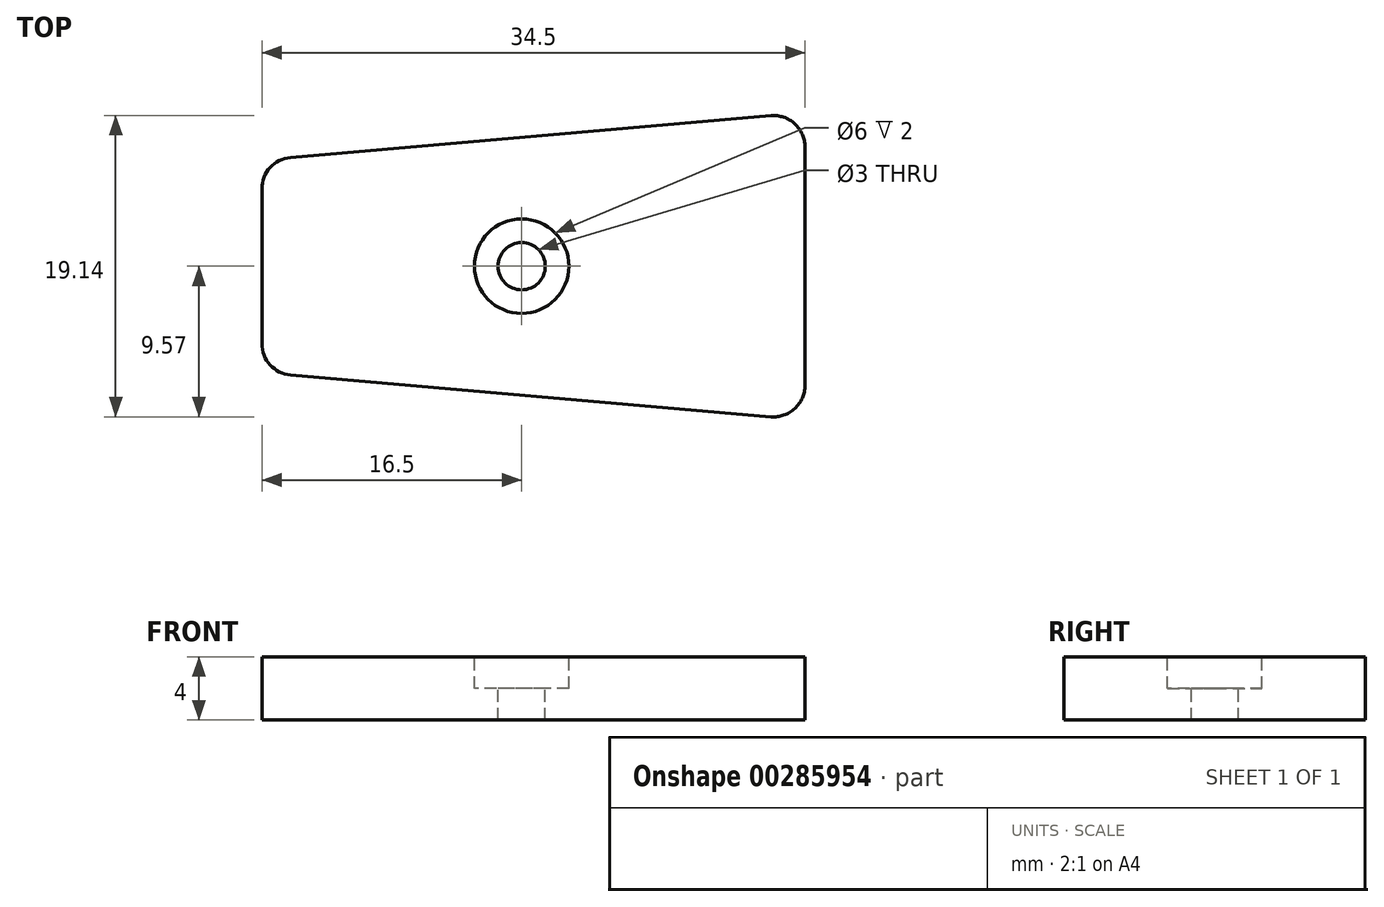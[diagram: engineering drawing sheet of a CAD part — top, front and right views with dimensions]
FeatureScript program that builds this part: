
annotation { "Feature Type Name" : "Feature", "Feature Type Description" : "" }
export const myFeature = defineFeature(function(context is Context, id is Id, definition is map)
    precondition{}
    {
        {
            var Q0;
            Q0=qCreatedBy(makeId("Top.planeOp"),FACE);
            var sketch = newSketch(context, id + "F0", { "sketchPlane" : qUnion([Q0])});
            skLineSegment(sketch, "E0", {"start": v(34.5, 19.5) * mm, "end": v(34.5, 0) * mm});
            skLineSegment(sketch, "E1", {"start": v(0, 3) * mm, "end": v(34.5, 0) * mm});
            skLineSegment(sketch, "E2", {"start": v(0, 16.5) * mm, "end": v(34.5, 19.5) * mm});
            skLineSegment(sketch, "E3", {"start": v(0, 16.5) * mm, "end": v(0, 3) * mm});
            skSolve(sketch);
        }
        {
            var Q0;
            Q0=makeQuery(id+"F0.imprint","IMPRINT",FACE,{"disambiguationData":[TD([[makeQuery(id+"F0.imprint","IMPRINT",EDGE,{"derivedFrom":sQuery(id+"F0.wireOp",EDGE,"E0")}),-1.0]])]});
            extrude(context, id + "F1", {"entities" : qUnion([Q0]), "depth" : 4 * mm});
        }
        {
            var Q0;
            Q0=makeQuery(id+"F1.opExtrude","CAP_FACE",FACE,{"disambiguationData":[OSD([sQuery(id+"F0.wireOp",EDGE,"E0"),sQuery(id+"F0.wireOp",EDGE,"E1"),sQuery(id+"F0.wireOp",EDGE,"E2"),sQuery(id+"F0.wireOp",EDGE,"E3")])],"isStart":false});
            var sketch = newSketch(context, id + "F2", { "sketchPlane" : qUnion([Q0])});
            skPoint(sketch, "E4", {"position": v(16.5, 9.75) * mm});
            skCircle(sketch, "E5", {"center": v(16.5, 9.75) * mm, "radius": 1.5 * mm});
            skCircle(sketch, "E6", {"center": v(16.5, 9.75) * mm, "radius": 3 * mm});
            skSolve(sketch);
        }
        {
            var Q0;
            Q0=makeQuery(id+"F2.imprint","IMPRINT",FACE,{"disambiguationData":[TD([[makeQuery(id+"F2.imprint","IMPRINT",EDGE,{"derivedFrom":sQuery(id+"F2.wireOp",EDGE,"E5")}),-1.0]])]});
            extrude(context, id + "F3", {"entities" : qUnion([Q0]), "operationType" : NewBodyOperationType.REMOVE, "oppositeDirection" : true, "depth" : 2 * mm});
        }
        {
            var Q0;
            Q0=makeQuery(id+"F3.boolean.opBoolean","SPLIT",FACE,{"disambiguationData":[TD([makeQuery(id+"F3.opExtrude","SWEPT_FACE",FACE,{"disambiguationData":[OSD([sQuery(id+"F2.wireOp",EDGE,"E5")])]})])],"derivedFrom":makeQuery(id+"F1.opExtrude","CAP_FACE",FACE,{"disambiguationData":[OSD([sQuery(id+"F0.wireOp",EDGE,"E0"),sQuery(id+"F0.wireOp",EDGE,"E1"),sQuery(id+"F0.wireOp",EDGE,"E2"),sQuery(id+"F0.wireOp",EDGE,"E3")])],"isStart":false})});
            extrude(context, id + "F4", {"entities" : qUnion([Q0]), "operationType" : NewBodyOperationType.REMOVE, "oppositeDirection" : true, "depth" : 4 * mm});
        }
        {
            var Q0;
            Q0=makeQuery(id+"F1.opExtrude","SWEPT_EDGE",EDGE,{"disambiguationData":[OSD([sQuery(id+"F0.wireOp",EDGE,"E0"),sQuery(id+"F0.wireOp",EDGE,"E1")])]});
            fillet(context, id + "F5", {"entities" : qUnion([Q0]), "radius" : 2 * mm, "tangentPropagation" : true, "allowEdgeOverflow" : false});
        }
        {
            var Q0;
            Q0=makeQuery(id+"F1.opExtrude","SWEPT_EDGE",EDGE,{"disambiguationData":[OSD([sQuery(id+"F0.wireOp",EDGE,"E0"),sQuery(id+"F0.wireOp",EDGE,"E2")])]});
            fillet(context, id + "F6", {"entities" : qUnion([Q0]), "radius" : 2 * mm, "tangentPropagation" : true, "allowEdgeOverflow" : false});
        }
        {
            var Q0;
            Q0=makeQuery(id+"F1.opExtrude","SWEPT_EDGE",EDGE,{"disambiguationData":[OSD([sQuery(id+"F0.wireOp",EDGE,"E2"),sQuery(id+"F0.wireOp",EDGE,"E3")])]});
            fillet(context, id + "F7", {"entities" : qUnion([Q0]), "radius" : 2 * mm, "tangentPropagation" : true, "allowEdgeOverflow" : false});
        }
        {
            var Q0;
            Q0=makeQuery(id+"F1.opExtrude","SWEPT_EDGE",EDGE,{"disambiguationData":[OSD([sQuery(id+"F0.wireOp",EDGE,"E1"),sQuery(id+"F0.wireOp",EDGE,"E3")])]});
            fillet(context, id + "F8", {"entities" : qUnion([Q0]), "radius" : 2 * mm, "tangentPropagation" : true, "allowEdgeOverflow" : false});
        }
    });
